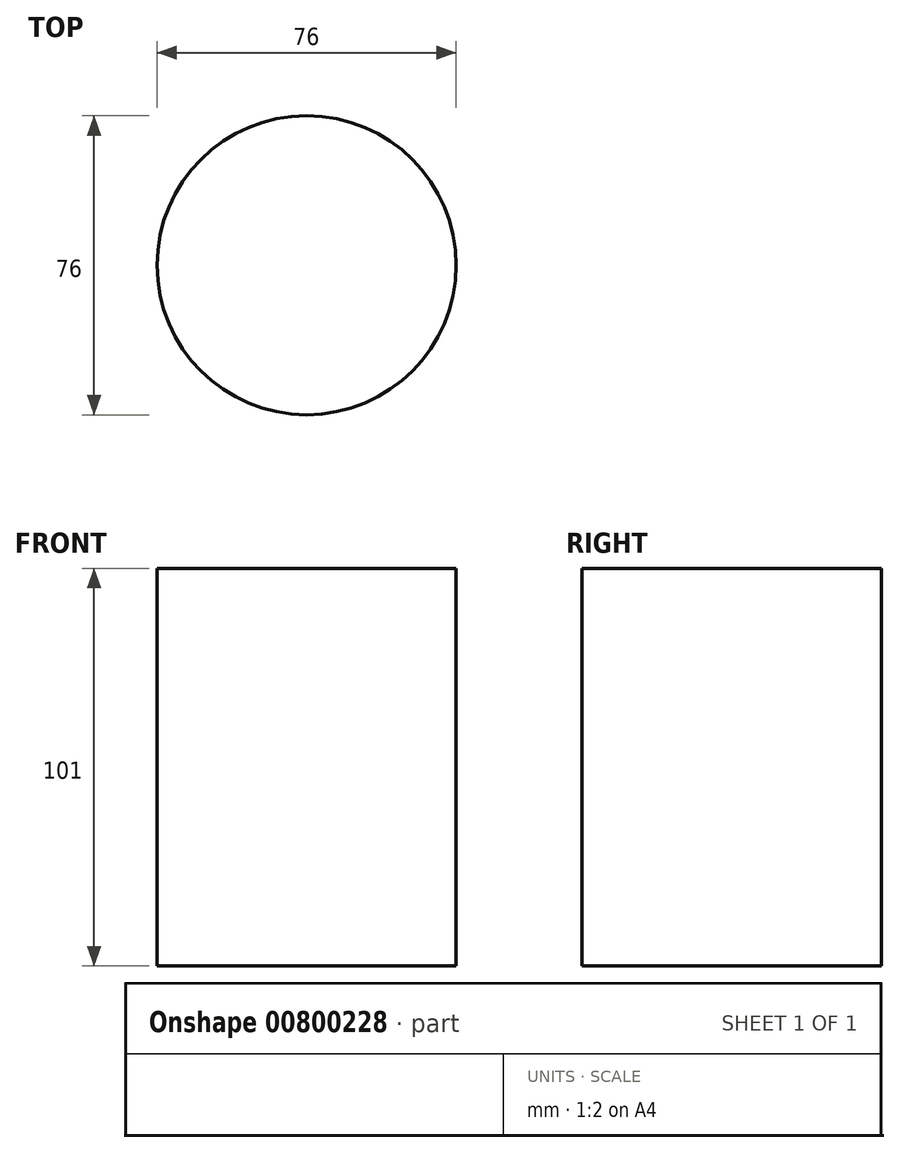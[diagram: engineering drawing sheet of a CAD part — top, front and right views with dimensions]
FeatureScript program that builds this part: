
annotation { "Feature Type Name" : "Feature", "Feature Type Description" : "" }
export const myFeature = defineFeature(function(context is Context, id is Id, definition is map)
    precondition{}
    {
        {
            var Q0;
            Q0=qCreatedBy(makeId("Top.planeOp"),FACE);
            var sketch = newSketch(context, id + "F0", { "sketchPlane" : qUnion([Q0])});
            skCircle(sketch, "E0", {"center": v(0, 0) * mm, "radius": 38 * mm});
            skSolve(sketch);
        }
        {
            var Q0;
            Q0=makeQuery(id+"F0.imprint","IMPRINT",FACE,{"disambiguationData":[TD([[makeQuery(id+"F0.imprint","IMPRINT",EDGE,{"derivedFrom":sQuery(id+"F0.wireOp",EDGE,"E0")}),1.0]])]});
            extrude(context, id + "F1", {"entities" : qUnion([Q0]), "depth" : 101 * mm, "offsetDistance" : 25 * mm});
        }
    });
